# Revit family: Single-Raised_Panel_with_SidelightsTransom
name_source: partatom
category: Doors
revit_build: Autodesk Revit 2013 (Build: 20120221_2030(x64)
units: mm (PartAtom-declared; Revit-internal decimal feet)

## types (7) — shared parameters
Analytic Construction = <None>
Assembly Code = C1020
Function = Interior
Rail Width - Base = 0' - 10"
Rail Width - Center = 0' - 7"
Rail Width - Top = 0' - 4"
Sidelight Width = 1' - 0"
Stile Width = 0' - 5"
Thickness = 0' - 2"
Threshold Projection = 0' - 1 3/4"
Transom Height = 1' - 0"
Trim Projection Ext = 0' - 1"
Trim Projection Int = 0' - 1"
Trim Width = 0' - 3"
Wall Closure = By host

## per-type parameters (varying)
| type | Door Material | Frame Material | Height | Kick Plate Deptth | Width |
| 30" x 84" | Door - Panel | Door - Frame | 7' - 0" | 0' - 6" | 2' - 6" |
| 30" x 80" | Door - Panel | Door - Frame | 6' - 8" | 0' - 4" | 2' - 6" |
| 32" x 84" | Door - Panel | Door - Frame | 7' - 0" | 0' - 4" | 2' - 8" |
| 34" x 84" | Door - Panel | Door - Frame | 7' - 0" | 0' - 4" | 2' - 10" |
| 34" x 80" | Door - Panel | Door - Frame | 6' - 8" | 0' - 4" | 2' - 10" |
| 36" x 80" | Door - Frame | Door - Frame | 6' - 8" | 0' - 4" | 3' - 0" |
| 36" x 80" w/ transom | Door - Panel | Door - Panel | 6' - 8" | 0' - 6" | 3' - 0" |

## geometry (parser evidence)
native form markers: Blend x4, Sweep x1
no freeform markers — native parametric forms only
